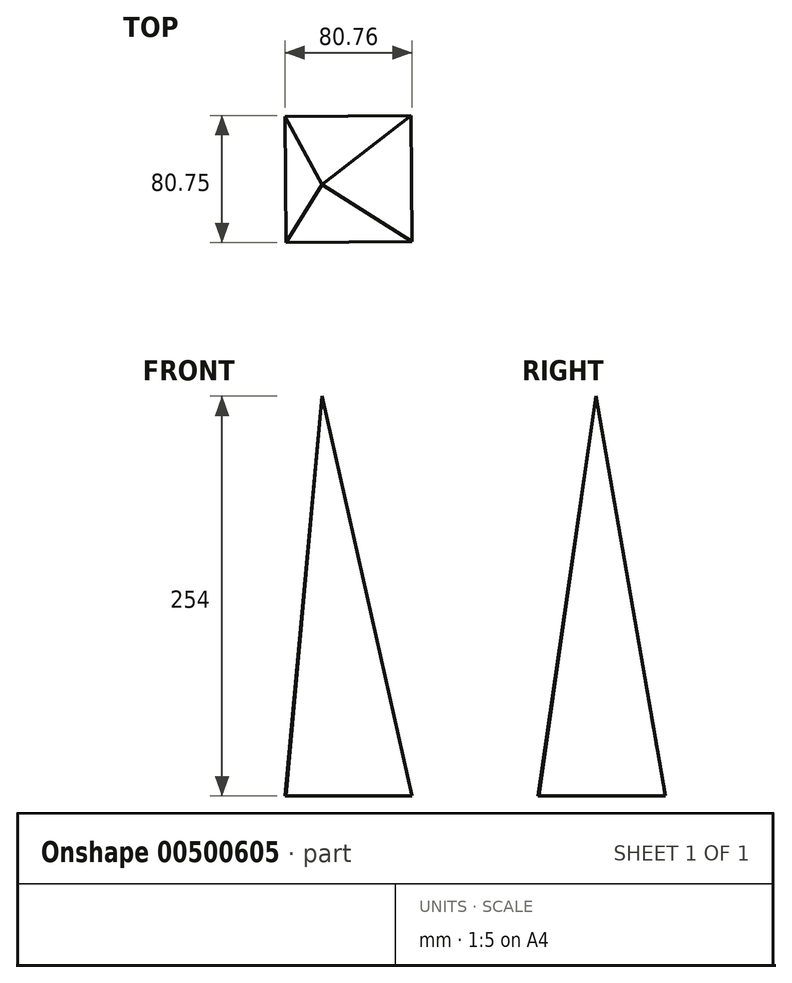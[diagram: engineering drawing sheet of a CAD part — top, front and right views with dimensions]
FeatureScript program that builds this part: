
annotation { "Feature Type Name" : "Feature", "Feature Type Description" : "" }
export const myFeature = defineFeature(function(context is Context, id is Id, definition is map)
    precondition{}
    {
        {
            var Q0;
            Q0=qCreatedBy(makeId("Top.planeOp"),FACE);
            var sketch = newSketch(context, id + "F0", { "sketchPlane" : qUnion([Q0])});
            skCircle(sketch, "E0.cCircle", {"center": v(0, 7.28) * mm, "radius": 56.58 * mm, "construction": true});
            skLineSegment(sketch, "E0.0", {"start": v(-40.38, 46.92) * mm, "end": v(39.64, 47.66) * mm});
            skLineSegment(sketch, "E0.1", {"start": v(39.64, 47.66) * mm, "end": v(40.38, -32.36) * mm});
            skLineSegment(sketch, "E0.2", {"start": v(40.38, -32.36) * mm, "end": v(-39.64, -33.1) * mm});
            skLineSegment(sketch, "E0.3", {"start": v(-39.64, -33.1) * mm, "end": v(-40.38, 46.92) * mm});
            skSolve(sketch);
        }
        {
            var Q0;
            Q0=qCreatedBy(makeId("Top.planeOp"),FACE);
            cPlane(context, id + "F1", {"entities" : qUnion([Q0]), "cplaneType" : CPlaneType.OFFSET, "offset" : 254 * mm, "width" : 152.4 * mm, "height" : 152.4 * mm});
        }
        {
            var Q0;
            Q0=qCreatedBy(id+"F1.planeOp",FACE);
            var sketch = newSketch(context, id + "F2", { "sketchPlane" : qUnion([Q0])});
            skPoint(sketch, "E1", {"position": v(-16.92, 3.67) * mm});
            skSolve(sketch);
        }
        {
            var Q0;
            Q0=sQuery(id+"F2.wireOp",VERTEX,"E1");
            var Q1;
            Q1=makeQuery(id+"F0.imprint","IMPRINT",FACE,{"disambiguationData":[TD([[makeQuery(id+"F0.imprint","IMPRINT",EDGE,{"derivedFrom":sQuery(id+"F0.wireOp",EDGE,"E0.0")}),-1.0]])]});
            loft(context, id + "F3", {"sheetProfilesArray" : [{ "sheetProfileEntities" : qUnion([Q0]) }, { "sheetProfileEntities" : qUnion([Q1]) }]});
        }
    });
